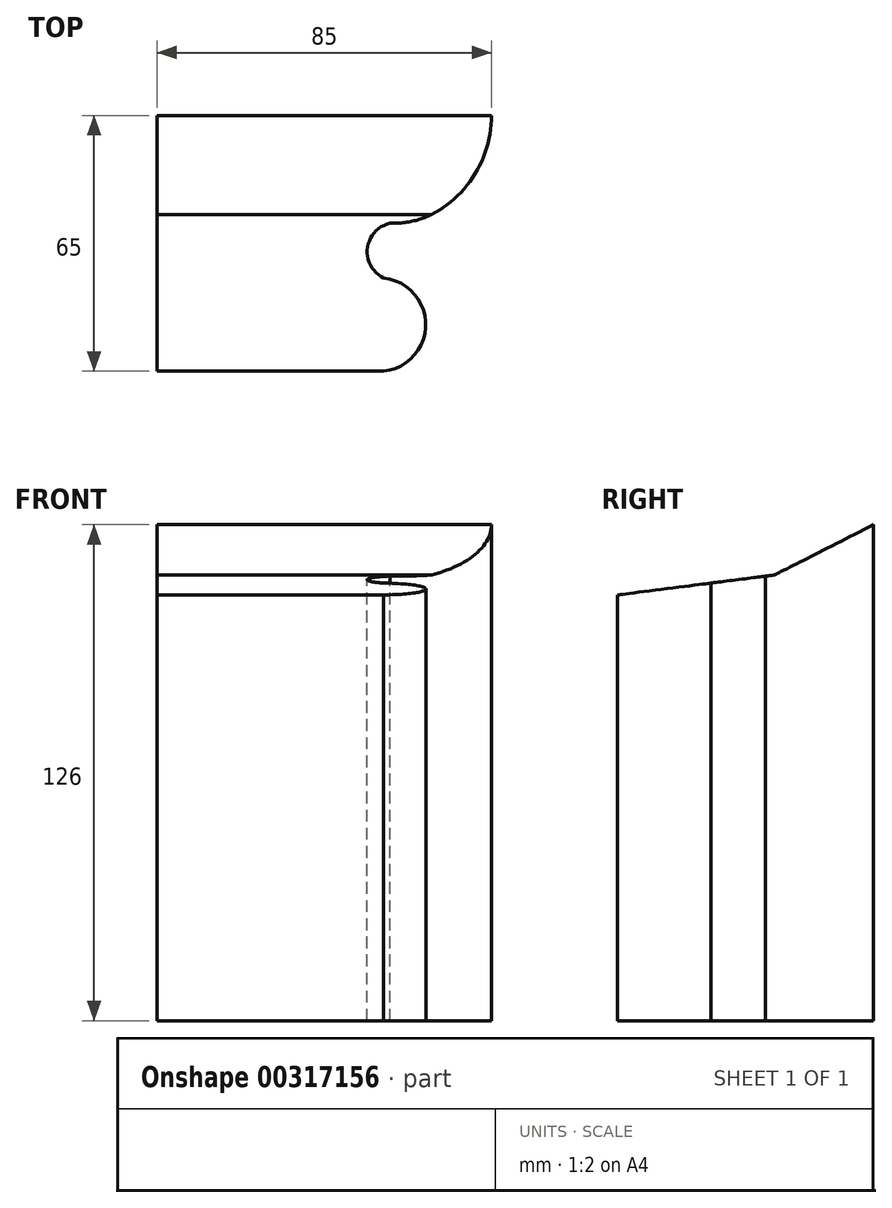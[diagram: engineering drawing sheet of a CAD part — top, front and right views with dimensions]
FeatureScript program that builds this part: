
annotation { "Feature Type Name" : "Feature", "Feature Type Description" : "" }
export const myFeature = defineFeature(function(context is Context, id is Id, definition is map)
    precondition{}
    {
        {
            var Q0;
            Q0=qCreatedBy(makeId("Front.planeOp"),FACE);
            var sketch = newSketch(context, id + "F0", { "sketchPlane" : qUnion([Q0])});
            skLineSegment(sketch, "E0.bottom", {"start": v(42.5, 63) * mm, "end": v(-42.5, 63) * mm});
            skLineSegment(sketch, "E0.top", {"start": v(42.5, -63) * mm, "end": v(-42.5, -63) * mm});
            skLineSegment(sketch, "E0.left", {"start": v(42.5, 63) * mm, "end": v(42.5, -63) * mm});
            skLineSegment(sketch, "E0.right", {"start": v(-42.5, 63) * mm, "end": v(-42.5, -63) * mm});
            skPoint(sketch, "E0.middle", {"position": v(0, 0) * mm});
            skSolve(sketch);
        }
        {
            var Q0;
            Q0=qSketchRegion(id+"F0",true);
            extrude(context, id + "F1", {"entities" : qUnion([Q0]), "depth" : 65 * mm});
        }
        {
            var Q0;
            Q0=makeQuery(id+"F1.opExtrude","SWEPT_FACE",FACE,{"disambiguationData":[OSD([sQuery(id+"F0.wireOp",EDGE,"E0.bottom")])]});
            var sketch = newSketch(context, id + "F2", { "sketchPlane" : qUnion([Q0])});
            skArc(sketch, "E1", {"start": v(30.14, -23.46) * mm, "mid": v(39.22, -13.26) * mm, "end": v(42.5, 0) * mm});
            skArc(sketch, "E2", {"start": v(16.65, -27.4) * mm, "mid": v(23.72, -26.54) * mm, "end": v(30.14, -23.46) * mm});
            skArc(sketch, "E3", {"start": v(16.65, -27.4) * mm, "mid": v(10.93, -33.8) * mm, "end": v(15.1, -41.3) * mm});
            skArc(sketch, "E4", {"start": v(15.1, -65) * mm, "mid": v(25.83, -53.15) * mm, "end": v(15.1, -41.3) * mm});
            skLineSegment(sketch, "E5", {"start": v(15.1, -65) * mm, "end": v(42.5, -65) * mm});
            skLineSegment(sketch, "E6", {"start": v(42.5, -65) * mm, "end": v(42.5, 0) * mm});
            skSolve(sketch);
        }
        {
            var Q0;
            Q0=qSketchRegion(id+"F2",true);
            extrude(context, id + "F3", {"entities" : qUnion([Q0]), "operationType" : NewBodyOperationType.REMOVE, "oppositeDirection" : true, "depth" : 200 * mm});
        }
        {
            var Q0;
            Q0=makeQuery(id+"F1.opExtrude","SWEPT_FACE",FACE,{"disambiguationData":[OSD([sQuery(id+"F0.wireOp",EDGE,"E0.right")])]});
            var sketch = newSketch(context, id + "F4", { "sketchPlane" : qUnion([Q0])});
            skLineSegment(sketch, "E7", {"start": v(0, 63) * mm, "end": v(25.15, 50.23) * mm});
            skLineSegment(sketch, "E8", {"start": v(25.15, 50.23) * mm, "end": v(65, 45.17) * mm});
            skLineSegment(sketch, "E9", {"start": v(65, 45.17) * mm, "end": v(65, 63) * mm});
            skLineSegment(sketch, "E10", {"start": v(65, 63) * mm, "end": v(0, 63) * mm});
            skSolve(sketch);
        }
        {
            var Q0;
            Q0 = qSketchRegion(id + "F4", true);
            extrude(context, id + "F5", {"entities" : qUnion([Q0]), "operationType" : NewBodyOperationType.REMOVE, "oppositeDirection" : true, "depth" : 100 * mm});
        }
    });
